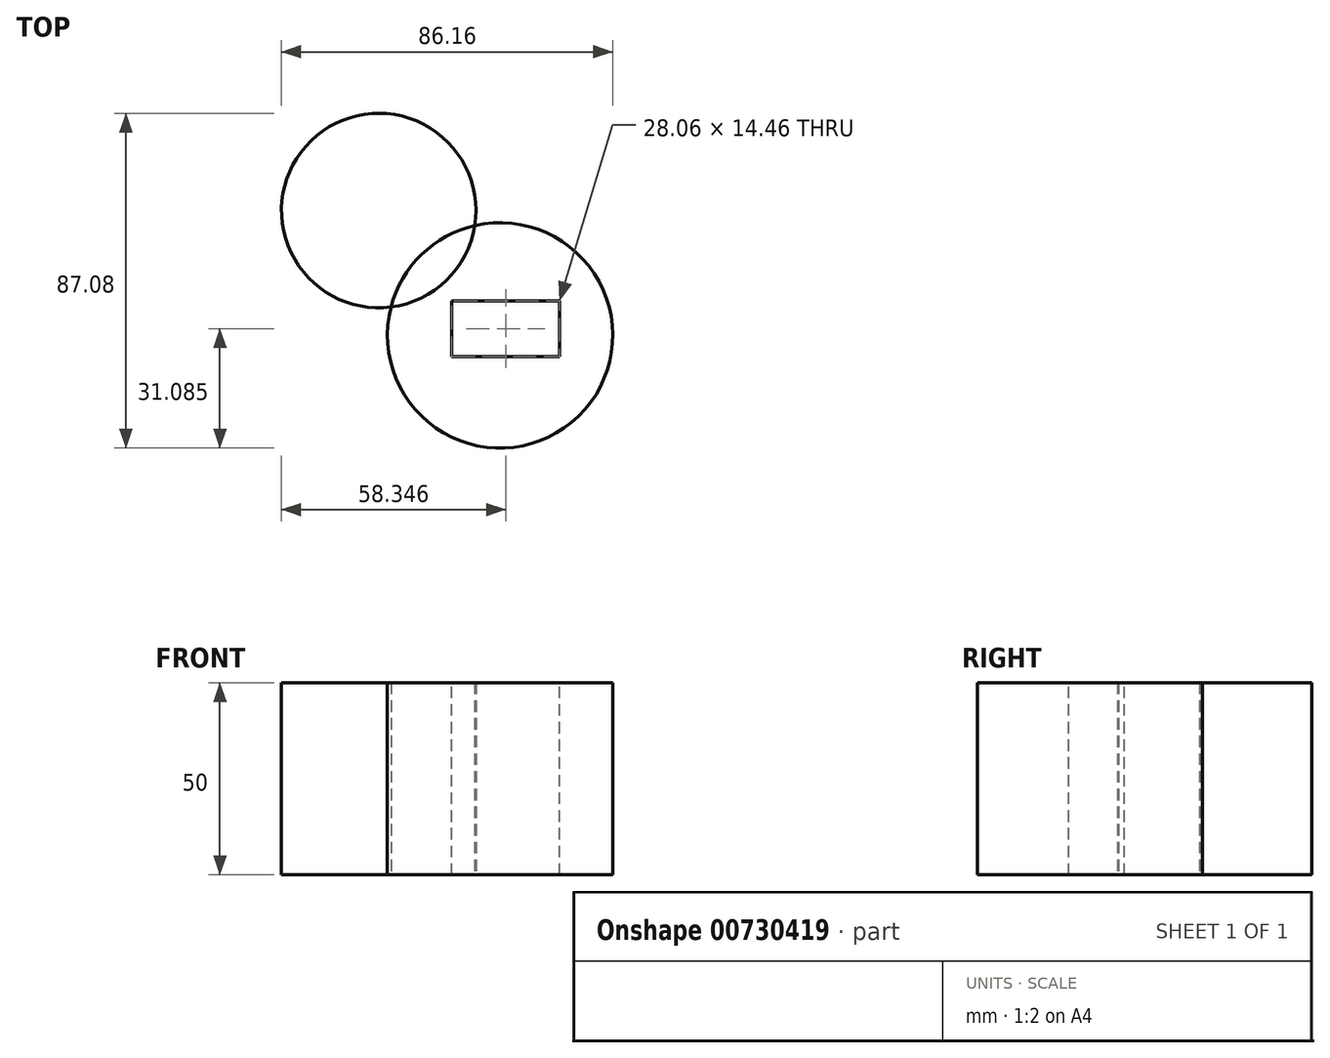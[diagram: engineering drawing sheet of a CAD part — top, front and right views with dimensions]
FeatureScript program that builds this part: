
annotation { "Feature Type Name" : "Feature", "Feature Type Description" : "" }
export const myFeature = defineFeature(function(context is Context, id is Id, definition is map)
    precondition{}
    {
        {
            var Q0;
            Q0=qCreatedBy(makeId("Top.planeOp"),FACE);
            var sketch = newSketch(context, id + "F0", { "sketchPlane" : qUnion([Q0])});
            skCircle(sketch, "E0", {"center": v(0, 0) * mm, "radius": 29.3 * mm});
            skCircle(sketch, "E1", {"center": v(-31.56, 32.48) * mm, "radius": 25.29 * mm});
            skSolve(sketch);
        }
        {
            var Q0;
            {var subQ0=sQuery(id+"F0.wireOp",EDGE,"E1");var subQ1=sQuery(id+"F0.wireOp",EDGE,"E0");var subQ2=makeQuery(id+"F0.imprint","INTERSECT",VERTEX,{"disambiguationData":[OD(0.0)],"derivedFrom":[subQ1,subQ0]});Q0=makeQuery(id+"F0.imprint","IMPRINT",FACE,{"disambiguationData":[TD([[makeQuery(id+"F0.imprint","IMPRINT",EDGE,{"disambiguationData":[TD([[subQ2,1.0]])],"derivedFrom":subQ1}),-1.0]])]});}
            var Q1;
            {var subQ0=sQuery(id+"F0.wireOp",EDGE,"E1");var subQ1=sQuery(id+"F0.wireOp",EDGE,"E0");var subQ2=makeQuery(id+"F0.imprint","INTERSECT",VERTEX,{"disambiguationData":[OD(0.0)],"derivedFrom":[subQ1,subQ0]});Q1=makeQuery(id+"F0.imprint","IMPRINT",FACE,{"disambiguationData":[TD([[makeQuery(id+"F0.imprint","IMPRINT",EDGE,{"disambiguationData":[TD([[subQ2,-1.0]])],"derivedFrom":subQ1}),1.0]])]});}
            extrude(context, id + "F1", {"entities" : qUnion([Q0, Q1]), "depth" : 50 * mm, "offsetDistance" : 25 * mm});
        }
        {
            var Q0;
            {var subQ0=sQuery(id+"F0.wireOp",EDGE,"E1");var subQ1=sQuery(id+"F0.wireOp",EDGE,"E0");var subQ2=makeQuery(id+"F0.imprint","INTERSECT",VERTEX,{"disambiguationData":[OD(0.0)],"derivedFrom":[subQ1,subQ0]});Q0=makeQuery(id+"F1.opExtrude","CAP_FACE",FACE,{"disambiguationData":[OSD([subQ1,subQ0]),TDD([makeQuery(id+"F0.imprint","IMPRINT",EDGE,{"disambiguationData":[TD([[subQ2,-1.0]])],"derivedFrom":subQ1}),makeQuery(id+"F0.imprint","IMPRINT",EDGE,{"disambiguationData":[TD([[subQ2,-1.0]])],"derivedFrom":subQ0})])],"isStart":false});}
            var sketch = newSketch(context, id + "F2", { "sketchPlane" : qUnion([Q0])});
            skLineSegment(sketch, "E2.bottom", {"start": v(-12.53, -5.46) * mm, "end": v(15.53, -5.46) * mm});
            skLineSegment(sketch, "E2.top", {"start": v(-12.53, 9) * mm, "end": v(15.53, 9) * mm});
            skLineSegment(sketch, "E2.left", {"start": v(-12.53, -5.46) * mm, "end": v(-12.53, 9) * mm});
            skLineSegment(sketch, "E2.right", {"start": v(15.53, -5.46) * mm, "end": v(15.53, 9) * mm});
            skSolve(sketch);
        }
        {
            var Q0;
            Q0=makeQuery(id+"F2.imprint","IMPRINT",FACE,{"disambiguationData":[TD([[makeQuery(id+"F2.imprint","IMPRINT",EDGE,{"derivedFrom":sQuery(id+"F2.wireOp",EDGE,"E2.bottom")}),1.0]])]});
            extrude(context, id + "F3", {"entities" : qUnion([Q0]), "operationType" : NewBodyOperationType.REMOVE, "oppositeDirection" : true, "depth" : 77 * mm, "offsetDistance" : 25 * mm});
        }
    });
